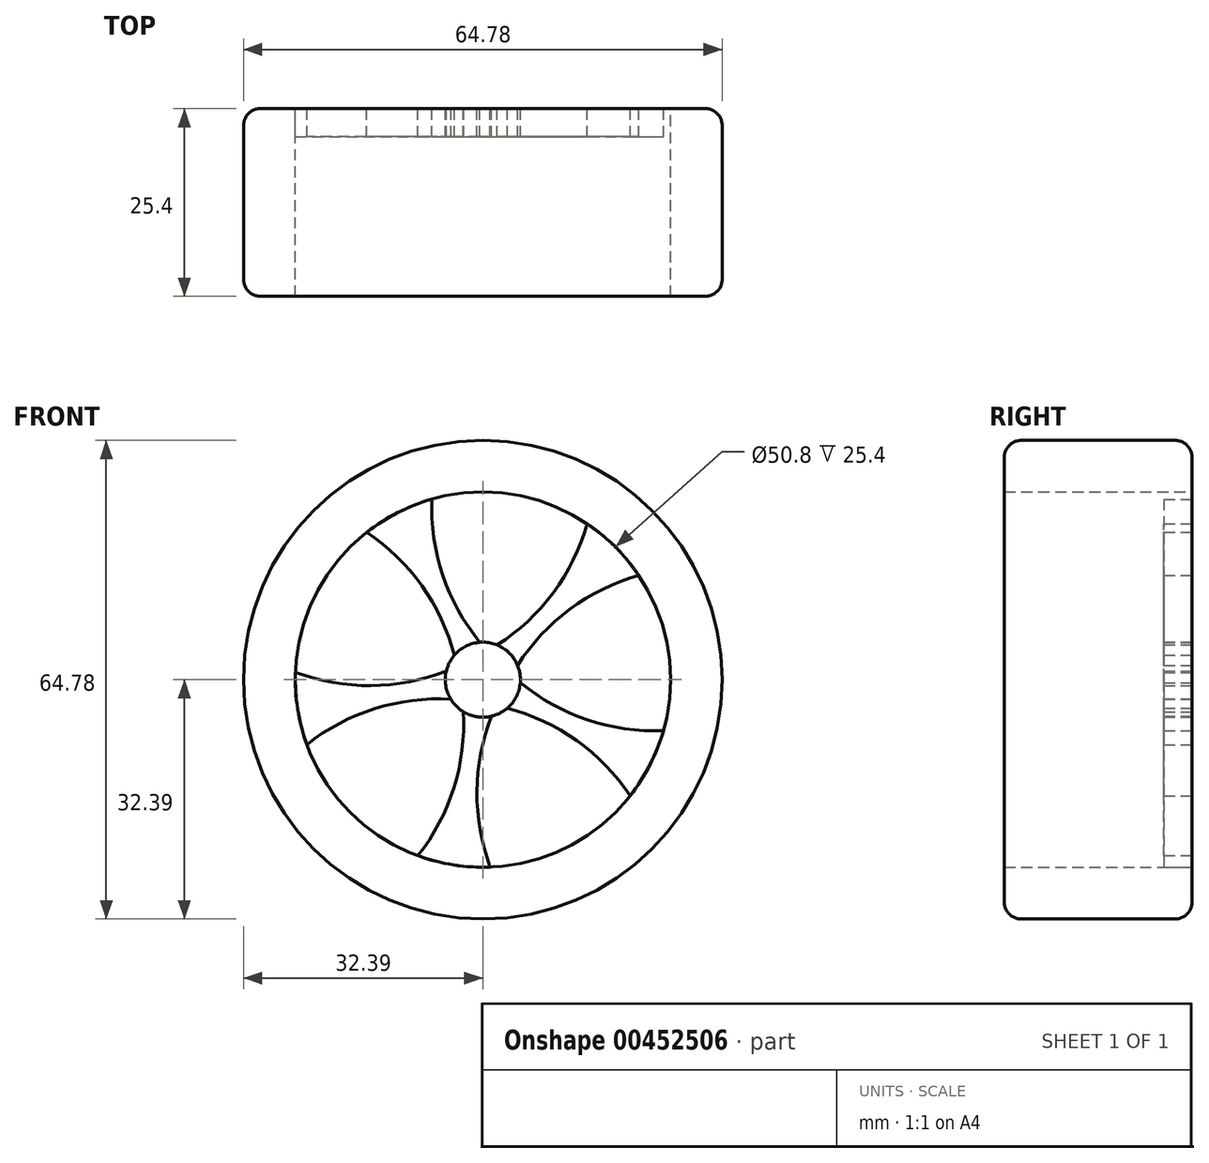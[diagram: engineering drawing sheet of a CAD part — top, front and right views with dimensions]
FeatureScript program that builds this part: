
annotation { "Feature Type Name" : "Feature", "Feature Type Description" : "" }
export const myFeature = defineFeature(function(context is Context, id is Id, definition is map)
    precondition{}
    {
        {
            var Q0;
            Q0=qCreatedBy(makeId("Front.planeOp"),FACE);
            var sketch = newSketch(context, id + "F0", { "sketchPlane" : qUnion([Q0])});
            skCircle(sketch, "E0", {"center": v(0, 0) * mm, "radius": 25.4 * mm});
            skCircle(sketch, "E1.0", {"center": v(0, 0) * mm, "radius": 27.3 * mm});
            skArc(sketch, "E2", {"start": v(25.4, 0) * mm, "mid": v(17.95, 17.95) * mm, "end": v(0, 25.4) * mm});
            skArc(sketch, "E3", {"start": v(17.95, 17.95) * mm, "mid": v(9.71, 23.45) * mm, "end": v(0, 25.4) * mm});
            skArc(sketch, "E4", {"start": v(17.95, 17.95) * mm, "mid": v(14.1, 21.1) * mm, "end": v(9.71, 23.45) * mm});
            skPoint(sketch, "E4.endSnap0", {"position": v(9.71, 23.45) * mm});
            skArc(sketch, "E5", {"start": v(25.4, 0) * mm, "mid": v(23.46, 9.71) * mm, "end": v(17.95, 17.95) * mm});
            skArc(sketch, "E6", {"start": v(23.46, 9.71) * mm, "mid": v(21.1, 14.1) * mm, "end": v(17.95, 17.95) * mm});
            skCircle(sketch, "E7.0", {"center": v(0, 0) * mm, "radius": 5.08 * mm});
            skArc(sketch, "E8", {"start": v(5.08, 0) * mm, "mid": v(3.6, 3.6) * mm, "end": v(0, 5.08) * mm});
            skArc(sketch, "E9", {"start": v(3.6, 3.6) * mm, "mid": v(1.95, 4.7) * mm, "end": v(0, 5.08) * mm});
            skPoint(sketch, "E9.startSnap0", {"position": v(3.6, 3.6) * mm});
            skArc(sketch, "E10", {"start": v(5.08, 0) * mm, "mid": v(4.7, 1.94) * mm, "end": v(3.6, 3.6) * mm});
            skArc(sketch, "E11", {"start": v(1.95, 4.7) * mm, "mid": v(9.54, 11.78) * mm, "end": v(14.1, 21.1) * mm});
            skPoint(sketch, "E11.startSnap0", {"position": v(1.95, 4.7) * mm});
            skArc(sketch, "E12", {"start": v(21.1, 14.1) * mm, "mid": v(11.78, 9.54) * mm, "end": v(4.7, 1.94) * mm});
            skArc(sketch, "E13.1.0", {"start": v(-3.86, 3.3) * mm, "mid": v(-8.25, 12.71) * mm, "end": v(-15.72, 19.93) * mm});
            skArc(sketch, "E13.1.1", {"start": v(-6.89, 24.43) * mm, "mid": v(-5.43, 14.15) * mm, "end": v(-0.4, 5.06) * mm});
            skArc(sketch, "E13.2.0", {"start": v(-4.33, -2.65) * mm, "mid": v(-14.64, -3.92) * mm, "end": v(-23.81, -8.79) * mm});
            skArc(sketch, "E13.2.1", {"start": v(-25.37, 1) * mm, "mid": v(-15.13, -0.8) * mm, "end": v(-4.94, 1.19) * mm});
            skArc(sketch, "E13.3.0", {"start": v(1.18, -4.94) * mm, "mid": v(-0.8, -15.13) * mm, "end": v(1, -25.36) * mm});
            skArc(sketch, "E13.3.1", {"start": v(-8.79, -23.82) * mm, "mid": v(-3.92, -14.64) * mm, "end": v(-2.65, -4.33) * mm});
            skArc(sketch, "E13.4.0", {"start": v(5.06, -0.4) * mm, "mid": v(14.15, -5.43) * mm, "end": v(24.43, -6.89) * mm});
            skArc(sketch, "E13.4.1", {"start": v(19.93, -15.72) * mm, "mid": v(12.71, -8.25) * mm, "end": v(3.3, -3.86) * mm});
            skArc(sketch, "E14", {"start": v(3.3, -3.86) * mm, "mid": v(4.52, -2.3) * mm, "end": v(5.06, -0.4) * mm});
            skArc(sketch, "E15", {"start": v(-2.65, -4.33) * mm, "mid": v(-0.8, -5.02) * mm, "end": v(1.18, -4.94) * mm});
            skArc(sketch, "E16", {"start": v(-4.94, 1.19) * mm, "mid": v(-5.02, -0.8) * mm, "end": v(-4.33, -2.65) * mm});
            skArc(sketch, "E17", {"start": v(-0.4, 5.06) * mm, "mid": v(-2.3, 4.53) * mm, "end": v(-3.86, 3.3) * mm});
            skArc(sketch, "E18", {"start": v(-6.89, 24.43) * mm, "mid": v(-11.52, 22.61) * mm, "end": v(-15.72, 19.93) * mm});
            skArc(sketch, "E19", {"start": v(-25.37, 1) * mm, "mid": v(-25.07, -3.97) * mm, "end": v(-23.81, -8.79) * mm});
            skArc(sketch, "E20", {"start": v(-8.79, -23.82) * mm, "mid": v(-3.97, -25.07) * mm, "end": v(1, -25.36) * mm});
            skArc(sketch, "E21", {"start": v(19.93, -15.72) * mm, "mid": v(22.6, -11.51) * mm, "end": v(24.43, -6.89) * mm});
            skCircle(sketch, "E22.0", {"center": v(0, 0) * mm, "radius": 32.39 * mm});
            skSolve(sketch);
        }
        {
            var Q0;
            Q0=makeQuery(id+"F0.imprint","IMPRINT",FACE,{"disambiguationData":[TD([[makeQuery(id+"F0.imprint","IMPRINT",EDGE,{"derivedFrom":sQuery(id+"F0.wireOp",EDGE,"E1.0")}),1.0]])]});
            extrude(context, id + "F1", {"entities" : qUnion([Q0]), "depth" : 25.4 * mm});
        }
        {
            var Q0;
            {var subQ0=sQuery(id+"F0.wireOp",EDGE,"E13.1.0");Q0=makeQuery(id+"F0.imprint","IMPRINT",FACE,{"disambiguationData":[TD([[makeQuery(id+"F0.imprint","IMPRINT",EDGE,{"derivedFrom":subQ0}),-1.0]])]});}
            var Q1;
            {var subQ0=sQuery(id+"F0.wireOp",EDGE,"E8");var subQ1=makeQuery(id+"F0.imprint","INTERSECT",VERTEX,{"derivedFrom":[subQ0,sQuery(id+"F0.wireOp",EDGE,"E10")]});Q1=makeQuery(id+"F0.imprint","IMPRINT",FACE,{"disambiguationData":[TD([[makeQuery(id+"F0.imprint","IMPRINT",EDGE,{"disambiguationData":[TD([[subQ1,1.0]])],"derivedFrom":subQ0}),-1.0]])]});}
            var Q2;
            {var subQ0=sQuery(id+"F0.wireOp",EDGE,"E13.4.0");Q2=makeQuery(id+"F0.imprint","IMPRINT",FACE,{"disambiguationData":[TD([[makeQuery(id+"F0.imprint","IMPRINT",EDGE,{"derivedFrom":subQ0}),-1.0]])]});}
            var Q3;
            {var subQ4=sQuery(id+"F0.wireOp",EDGE,"E13.3.0");Q3=makeQuery(id+"F0.imprint","IMPRINT",FACE,{"disambiguationData":[TD([[makeQuery(id+"F0.imprint","IMPRINT",EDGE,{"derivedFrom":subQ4}),-1.0]])]});}
            var Q4;
            {var subQ0=sQuery(id+"F0.wireOp",EDGE,"E13.2.0");Q4=makeQuery(id+"F0.imprint","IMPRINT",FACE,{"disambiguationData":[TD([[makeQuery(id+"F0.imprint","IMPRINT",EDGE,{"derivedFrom":subQ0}),-1.0]])]});}
            extrude(context, id + "F2", {"entities" : qUnion([Q0, Q1, Q2, Q3, Q4]), "depth" : 3.8 * mm});
        }
        {
            var Q0;
            {var subQ5=sQuery(id+"F0.wireOp",EDGE,"E9");Q0=makeQuery(id+"F0.imprint","IMPRINT",FACE,{"disambiguationData":[TD([[makeQuery(id+"F0.imprint","IMPRINT",EDGE,{"derivedFrom":subQ5}),1.0]])]});}
            extrude(context, id + "F3", {"entities" : qUnion([Q0]), "operationType" : NewBodyOperationType.ADD, "depth" : 3.8 * mm});
        }
        {
            var Q0;
            Q0=makeQuery(id+"F0.imprint","IMPRINT",FACE,{"disambiguationData":[TD([[makeQuery(id+"F0.imprint","IMPRINT",EDGE,{"derivedFrom":sQuery(id+"F0.wireOp",EDGE,"E1.0")}),-1.0]])]});
            extrude(context, id + "F4", {"entities" : qUnion([Q0]), "operationType" : NewBodyOperationType.ADD, "depth" : 25.4 * mm});
        }
        {
            var Q0;
            Q0=makeQuery(id+"F4.opExtrude","CAP_EDGE",EDGE,{"disambiguationData":[OSD([sQuery(id+"F0.wireOp",EDGE,"E22.0")])],"isStart":true});
            var Q1;
            Q1=makeQuery(id+"F4.opExtrude","CAP_EDGE",EDGE,{"disambiguationData":[OSD([sQuery(id+"F0.wireOp",EDGE,"E22.0")])],"isStart":false});
            fillet(context, id + "F5", {"entities" : qUnion([Q0, Q1]), "radius" : 2.3 * mm, "tangentPropagation" : true, "allowEdgeOverflow" : false});
        }
    });
